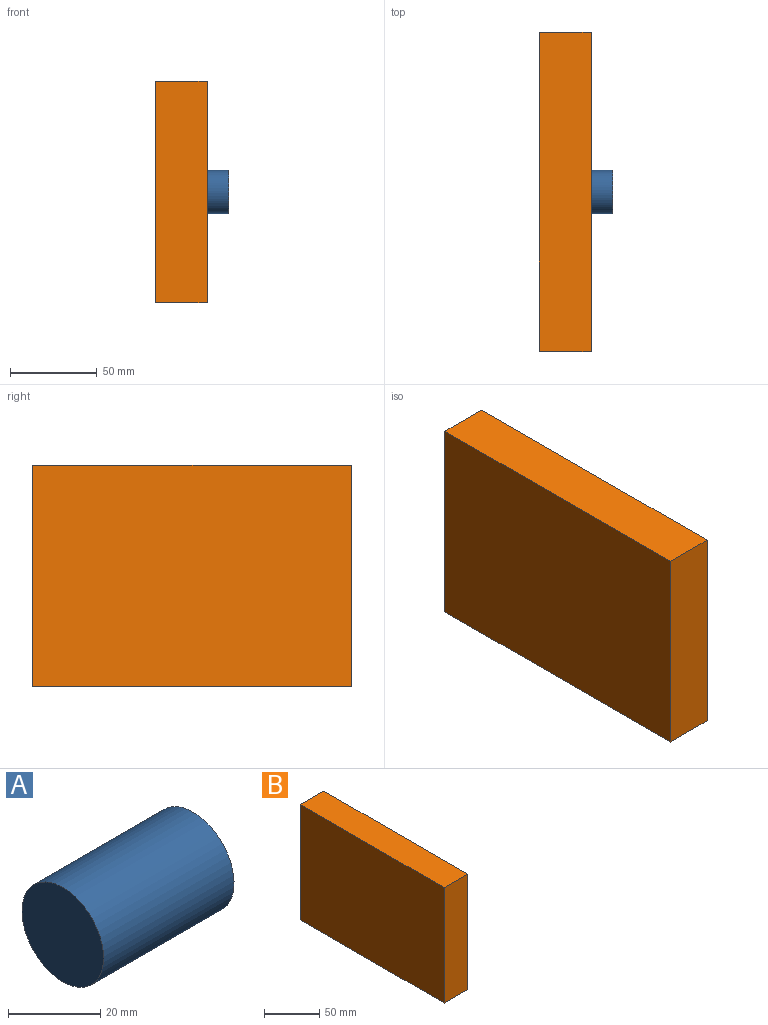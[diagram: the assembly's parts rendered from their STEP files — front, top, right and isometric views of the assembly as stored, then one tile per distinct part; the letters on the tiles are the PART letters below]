
ASSEMBLY  parts=2 mates=1
PART A: 3 faces, bbox 40x25x25 mm
  f0: cylinder r=12.52mm len=40mm, axis (-1,0,0), area 3146.3mm2, adj f1,f2
  f1: plane 25.04x25.04mm, normal (1,0,0), area 492.3mm2, adj f0
  f2: plane 25.04x25.04mm, normal (-1,0,0), area 492.3mm2, adj f0
PART B: 11 faces, bbox 30x184x127.7 mm
  f0: plane 184.04x127.66mm, normal (1,0,0), area 1533.5mm2, adj f1,f2,f3,f4,f6,f7,f8,f9
  f1: plane 184.04x30mm, normal (0,0,1), area 5521.3mm2, adj f0,f2,f4,f5
  f2: plane 127.66x30mm, normal (0,-1,0), area 3829.8mm2, adj f0,f1,f3,f5
  f3: plane 184.04x30mm, normal (0,0,-1), area 5521.3mm2, adj f0,f2,f4,f5
  f4: plane 127.66x30mm, normal (0,1,0), area 3829.8mm2, adj f0,f1,f3,f5
  f5: plane 184.04x127.66mm, normal (-1,0,0), area 23495.2mm2, adj f1,f2,f3,f4
  f6: plane 179.04x27.5mm, normal (0,0,-1), area 4923.7mm2, adj f0,f7,f9,f10
  f7: plane 122.66x27.5mm, normal (0,1,0), area 3373.2mm2, adj f0,f6,f8,f10
  f8: plane 179.04x27.5mm, normal (0,0,1), area 4923.7mm2, adj f0,f7,f9,f10
  f9: plane 122.66x27.5mm, normal (0,-1,0), area 3373.2mm2, adj f0,f6,f8,f10
  f10: plane 179.04x122.66mm, normal (1,0,0), area 21961.6mm2, adj f6,f7,f8,f9
PLACE A rot(axis=(1,0,0),90deg) t=(-70.76,-30.05,5.38)mm
PLACE B t=(-73.26,-30.05,5.38)mm
MATE slider A.f0 <-> B.f10  axis (-1,0,0) through (-70.76,-30.05,5.38)mm
